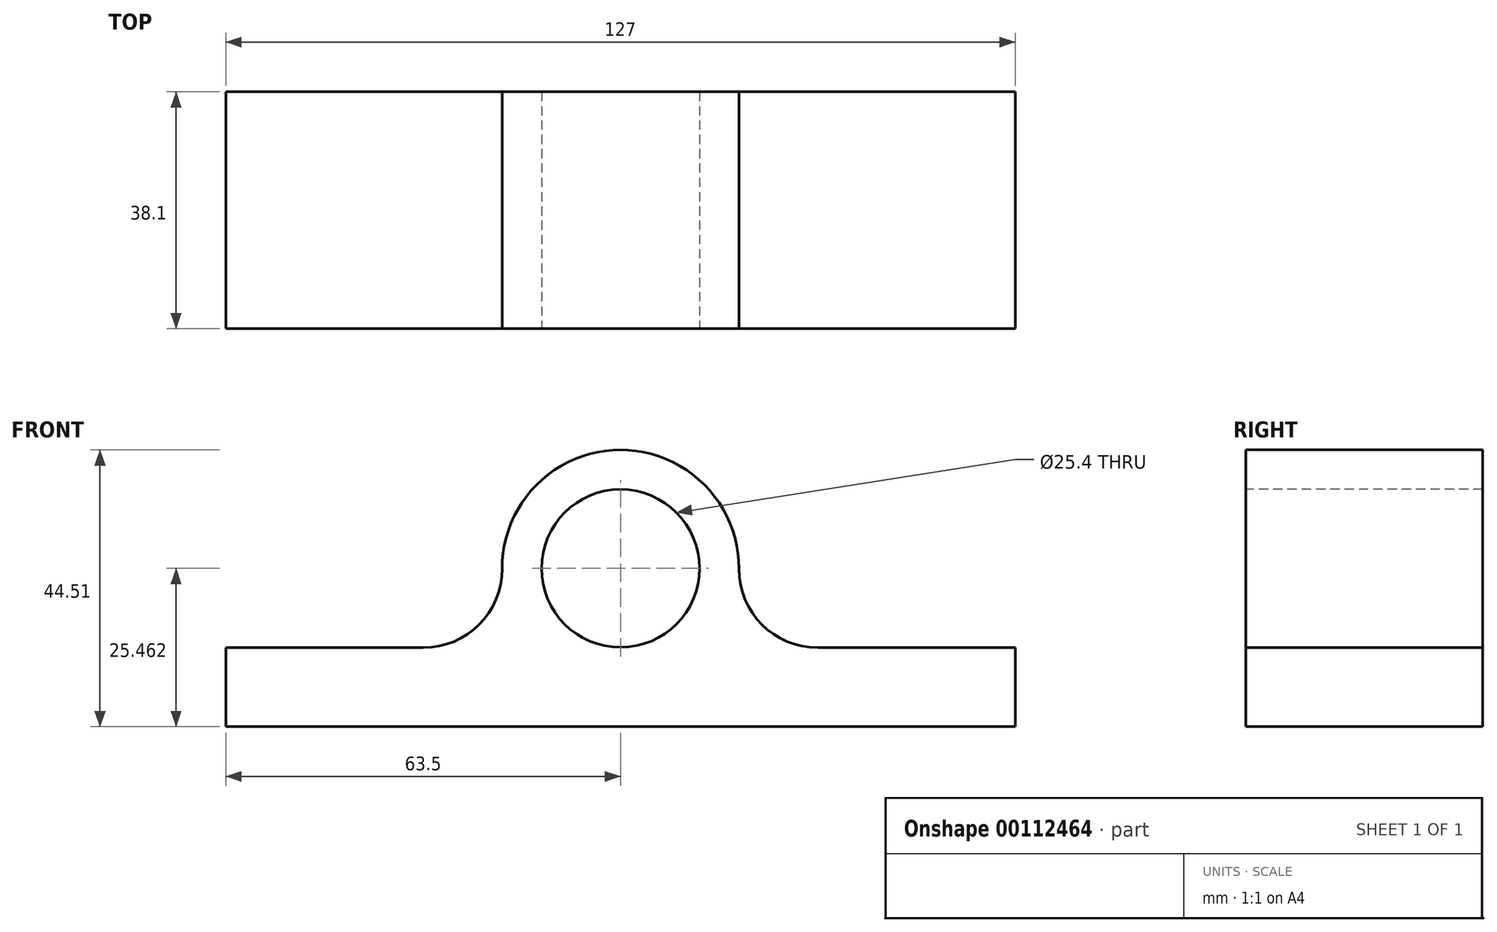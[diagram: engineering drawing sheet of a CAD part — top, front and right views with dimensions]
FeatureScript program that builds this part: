
annotation { "Feature Type Name" : "Feature", "Feature Type Description" : "" }
export const myFeature = defineFeature(function(context is Context, id is Id, definition is map)
    precondition{}
    {
        {
            var Q0;
            Q0=qCreatedBy(makeId("Front.planeOp"),FACE);
            var sketch = newSketch(context, id + "F0", { "sketchPlane" : qUnion([Q0])});
            skLineSegment(sketch, "E0", {"start": v(0, 0) * mm, "end": v(63.5, 0) * mm});
            skLineSegment(sketch, "E1", {"start": v(0, 0) * mm, "end": v(-63.5, 0) * mm});
            skLineSegment(sketch, "E2", {"start": v(-63.5, 0) * mm, "end": v(-63.5, 12.7) * mm});
            skLineSegment(sketch, "E3", {"start": v(63.5, 12.7) * mm, "end": v(63.5, 0) * mm});
            skLineSegment(sketch, "E4", {"start": v(-63.5, 12.7) * mm, "end": v(-31.75, 12.7) * mm});
            skLineSegment(sketch, "E5", {"start": v(63.5, 12.7) * mm, "end": v(31.75, 12.7) * mm});
            skPoint(sketch, "E6.visualSharp", {"position": v(-19.05, 12.7) * mm});
            skArc(sketch, "E6.filletArc", {"start": v(-31.75, 12.7) * mm, "mid": v(-22.77, 16.42) * mm, "end": v(-19.05, 25.4) * mm});
            skPoint(sketch, "E7.visualSharp", {"position": v(19.05, 12.7) * mm});
            skArc(sketch, "E7.filletArc", {"start": v(19.05, 25.4) * mm, "mid": v(22.77, 16.42) * mm, "end": v(31.75, 12.7) * mm});
            skArc(sketch, "E8", {"start": v(19.05, 25.4) * mm, "mid": v(0, 44.51) * mm, "end": v(-19.05, 25.4) * mm});
            skCircle(sketch, "E9", {"center": v(0, 25.46) * mm, "radius": 12.7 * mm});
            skSolve(sketch);
        }
        {
            var Q0;
            Q0=makeQuery(id+"F0.imprint","IMPRINT",FACE,{"disambiguationData":[TD([[makeQuery(id+"F0.imprint","IMPRINT",EDGE,{"derivedFrom":sQuery(id+"F0.wireOp",EDGE,"E0")}),1.0]])]});
            extrude(context, id + "F1", {"entities" : qUnion([Q0]), "oppositeDirection" : true, "depth" : 38.1 * mm});
        }
    });
